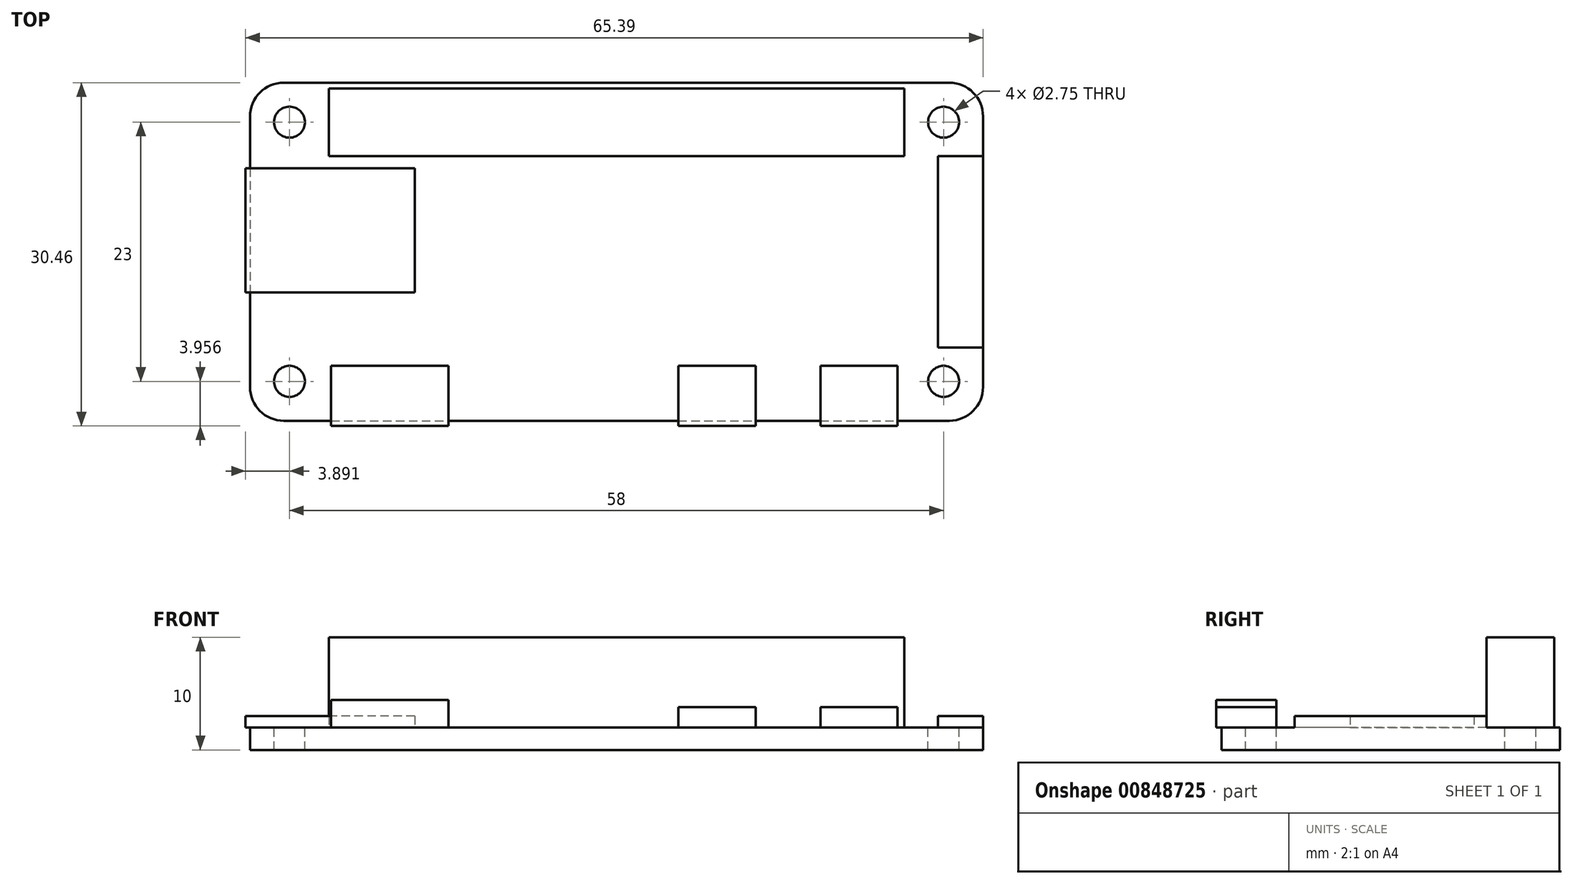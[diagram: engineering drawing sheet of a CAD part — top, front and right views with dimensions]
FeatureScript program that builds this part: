
annotation { "Feature Type Name" : "Feature", "Feature Type Description" : "" }
export const myFeature = defineFeature(function(context is Context, id is Id, definition is map)
    precondition{}
    {
        {
            var Q0;
            Q0=qCreatedBy(makeId("Top.planeOp"),FACE);
            var sketch = newSketch(context, id + "F0", { "sketchPlane" : qUnion([Q0])});
            skLineSegment(sketch, "E0.bottom", {"start": v(-40.48, 33.22) * mm, "end": v(24.52, 33.22) * mm});
            skLineSegment(sketch, "E0.top", {"start": v(-40.48, 3.22) * mm, "end": v(24.52, 3.22) * mm});
            skLineSegment(sketch, "E0.left", {"start": v(-40.48, 33.22) * mm, "end": v(-40.48, 3.22) * mm});
            skLineSegment(sketch, "E0.right", {"start": v(24.52, 33.22) * mm, "end": v(24.52, 3.22) * mm});
            skSolve(sketch);
        }
        {
            assignVariable(context, id + "F1", {"name" : "boardThickness", "anyValue" : 2});
        }
        {
            var Q0;
            Q0=makeQuery(id+"F0.imprint","IMPRINT",FACE,{"disambiguationData":[TD([[makeQuery(id+"F0.imprint","IMPRINT",EDGE,{"derivedFrom":sQuery(id+"F0.wireOp",EDGE,"E0.bottom")}),-1.0]])]});
            extrude(context, id + "F2", {"entities" : qUnion([Q0]), "depth" : (getVariable(context, 'boardThickness')) * mm, "offsetDistance" : 25 * mm});
        }
        {
            var Q0;
            Q0=makeQuery(id+"F2.opExtrude","SWEPT_EDGE",EDGE,{"disambiguationData":[OSD([sQuery(id+"F0.wireOp",EDGE,"E0.bottom"),sQuery(id+"F0.wireOp",EDGE,"E0.left")])]});
            var Q1;
            Q1=makeQuery(id+"F2.opExtrude","SWEPT_EDGE",EDGE,{"disambiguationData":[OSD([sQuery(id+"F0.wireOp",EDGE,"E0.top"),sQuery(id+"F0.wireOp",EDGE,"E0.left")])]});
            var Q2;
            Q2=makeQuery(id+"F2.opExtrude","SWEPT_EDGE",EDGE,{"disambiguationData":[OSD([sQuery(id+"F0.wireOp",EDGE,"E0.top"),sQuery(id+"F0.wireOp",EDGE,"E0.right")])]});
            var Q3;
            Q3=makeQuery(id+"F2.opExtrude","SWEPT_EDGE",EDGE,{"disambiguationData":[OSD([sQuery(id+"F0.wireOp",EDGE,"E0.bottom"),sQuery(id+"F0.wireOp",EDGE,"E0.right")])]});
            fillet(context, id + "F3", {"entities" : qUnion([Q0, Q1, Q2, Q3]), "radius" : 3 * mm, "tangentPropagation" : true, "allowEdgeOverflow" : false});
        }
        {
            var Q0;
            Q0=makeQuery(id+"F2.opExtrude","CAP_FACE",FACE,{"disambiguationData":[OSD([sQuery(id+"F0.wireOp",EDGE,"E0.bottom"),sQuery(id+"F0.wireOp",EDGE,"E0.top"),sQuery(id+"F0.wireOp",EDGE,"E0.left"),sQuery(id+"F0.wireOp",EDGE,"E0.right")])],"isStart":false});
            var sketch = newSketch(context, id + "F4", { "sketchPlane" : qUnion([Q0])});
            skCircle(sketch, "E1", {"center": v(21.02, 6.72) * mm, "radius": 1.38 * mm});
            skCircle(sketch, "E2", {"center": v(21.02, 29.72) * mm, "radius": 1.38 * mm});
            skCircle(sketch, "E3", {"center": v(-36.98, 29.72) * mm, "radius": 1.38 * mm});
            skCircle(sketch, "E4", {"center": v(-36.98, 6.72) * mm, "radius": 1.38 * mm});
            skCircle(sketch, "E5", {"center": v(21.02, 29.72) * mm, "radius": 3 * mm});
            skCircle(sketch, "E6", {"center": v(21.02, 6.72) * mm, "radius": 3 * mm});
            skCircle(sketch, "E7", {"center": v(-36.98, 6.72) * mm, "radius": 3 * mm});
            skCircle(sketch, "E8", {"center": v(-36.98, 29.72) * mm, "radius": 3 * mm});
            skSolve(sketch);
        }
        {
            var Q0;
            Q0=makeQuery(id+"F4.imprint","IMPRINT",FACE,{"disambiguationData":[TD([[makeQuery(id+"F4.imprint","IMPRINT",EDGE,{"derivedFrom":sQuery(id+"F4.wireOp",EDGE,"E2")}),1.0]])]});
            var Q1;
            Q1=makeQuery(id+"F4.imprint","IMPRINT",FACE,{"disambiguationData":[TD([[makeQuery(id+"F4.imprint","IMPRINT",EDGE,{"derivedFrom":sQuery(id+"F4.wireOp",EDGE,"E4")}),1.0]])]});
            var Q2;
            Q2=makeQuery(id+"F4.imprint","IMPRINT",FACE,{"disambiguationData":[TD([[makeQuery(id+"F4.imprint","IMPRINT",EDGE,{"derivedFrom":sQuery(id+"F4.wireOp",EDGE,"E3")}),1.0]])]});
            var Q3;
            Q3=makeQuery(id+"F4.imprint","IMPRINT",FACE,{"disambiguationData":[TD([[makeQuery(id+"F4.imprint","IMPRINT",EDGE,{"derivedFrom":sQuery(id+"F4.wireOp",EDGE,"E1")}),1.0]])]});
            extrude(context, id + "F5", {"entities" : qUnion([Q0, Q1, Q2, Q3]), "operationType" : NewBodyOperationType.REMOVE, "oppositeDirection" : true, "depth" : (getVariable(context, 'boardThickness')) * mm, "offsetDistance" : 25 * mm});
        }
        {
            assignVariable(context, id + "F6", {"name" : "miniHDMIh", "anyValue" : 2.42});
        }
        {
            assignVariable(context, id + "F7", {"name" : "microUSBh", "anyValue" : 1.8});
        }
        {
            var Q0;
            Q0=makeQuery(id+"F2.opExtrude","CAP_FACE",FACE,{"disambiguationData":[OSD([sQuery(id+"F0.wireOp",EDGE,"E0.bottom"),sQuery(id+"F0.wireOp",EDGE,"E0.top"),sQuery(id+"F0.wireOp",EDGE,"E0.left"),sQuery(id+"F0.wireOp",EDGE,"E0.right")])],"isStart":false});
            var sketch = newSketch(context, id + "F8", { "sketchPlane" : qUnion([Q0])});
            skLineSegment(sketch, "E9.bottom", {"start": v(-22.87, 2.76) * mm, "end": v(-33.29, 2.76) * mm});
            skLineSegment(sketch, "E9.top", {"start": v(-22.87, 8.09) * mm, "end": v(-33.29, 8.09) * mm});
            skLineSegment(sketch, "E9.left", {"start": v(-22.87, 2.76) * mm, "end": v(-22.87, 8.09) * mm});
            skLineSegment(sketch, "E9.right", {"start": v(-33.29, 2.76) * mm, "end": v(-33.29, 8.09) * mm});
            skPoint(sketch, "E9.middle", {"position": v(-28.08, 5.42) * mm});
            skLineSegment(sketch, "E10.bottom", {"start": v(16.95, 2.76) * mm, "end": v(10.1, 2.76) * mm});
            skLineSegment(sketch, "E10.top", {"start": v(16.95, 8.09) * mm, "end": v(10.1, 8.09) * mm});
            skLineSegment(sketch, "E10.left", {"start": v(16.95, 2.76) * mm, "end": v(16.95, 8.09) * mm});
            skLineSegment(sketch, "E10.right", {"start": v(10.1, 2.76) * mm, "end": v(10.1, 8.09) * mm});
            skPoint(sketch, "E10.middle", {"position": v(13.52, 5.42) * mm});
            skLineSegment(sketch, "E11.bottom", {"start": v(4.35, 2.76) * mm, "end": v(-2.5, 2.76) * mm});
            skLineSegment(sketch, "E11.top", {"start": v(4.35, 8.09) * mm, "end": v(-2.5, 8.09) * mm});
            skLineSegment(sketch, "E11.left", {"start": v(4.35, 2.76) * mm, "end": v(4.35, 8.09) * mm});
            skLineSegment(sketch, "E11.right", {"start": v(-2.5, 2.76) * mm, "end": v(-2.5, 8.09) * mm});
            skPoint(sketch, "E11.middle", {"position": v(0.92, 5.42) * mm});
            skLineSegment(sketch, "E12.bottom", {"start": v(-25.87, 14.62) * mm, "end": v(-40.87, 14.62) * mm});
            skLineSegment(sketch, "E12.top", {"start": v(-25.87, 25.62) * mm, "end": v(-40.87, 25.62) * mm});
            skLineSegment(sketch, "E12.left", {"start": v(-25.87, 14.62) * mm, "end": v(-25.87, 25.62) * mm});
            skLineSegment(sketch, "E12.right", {"start": v(-40.87, 14.62) * mm, "end": v(-40.87, 25.62) * mm});
            skPoint(sketch, "E12.middle", {"position": v(-33.37, 20.12) * mm});
            skLineSegment(sketch, "E13.bottom", {"start": v(20.52, 26.71) * mm, "end": v(24.52, 26.71) * mm});
            skLineSegment(sketch, "E13.top", {"start": v(20.52, 9.71) * mm, "end": v(24.52, 9.71) * mm});
            skLineSegment(sketch, "E13.left", {"start": v(20.52, 26.71) * mm, "end": v(20.52, 9.71) * mm});
            skLineSegment(sketch, "E13.right", {"start": v(24.52, 26.71) * mm, "end": v(24.52, 9.71) * mm});
            skSolve(sketch);
        }
        {
            var Q0;
            {var subQ0=sQuery(id+"F8.wireOp",EDGE,"E9.top");Q0=makeQuery(id+"F8.imprint","IMPRINT",FACE,{"disambiguationData":[TD([[makeQuery(id+"F8.imprint","IMPRINT",EDGE,{"derivedFrom":subQ0}),1.0]])]});}
            var Q1;
            {var subQ0=sQuery(id+"F8.wireOp",EDGE,"E9.bottom");Q1=makeQuery(id+"F8.imprint","IMPRINT",FACE,{"disambiguationData":[TD([[makeQuery(id+"F8.imprint","IMPRINT",EDGE,{"derivedFrom":subQ0}),-1.0]])]});}
            extrude(context, id + "F9", {"entities" : qUnion([Q0, Q1]), "operationType" : NewBodyOperationType.ADD, "depth" : (getVariable(context, 'miniHDMIh')) * mm, "offsetDistance" : 25 * mm});
        }
        {
            var Q0;
            {var subQ0=sQuery(id+"F8.wireOp",EDGE,"E11.top");Q0=makeQuery(id+"F8.imprint","IMPRINT",FACE,{"disambiguationData":[TD([[makeQuery(id+"F8.imprint","IMPRINT",EDGE,{"derivedFrom":subQ0}),1.0]])]});}
            var Q1;
            {var subQ0=sQuery(id+"F8.wireOp",EDGE,"E10.top");Q1=makeQuery(id+"F8.imprint","IMPRINT",FACE,{"disambiguationData":[TD([[makeQuery(id+"F8.imprint","IMPRINT",EDGE,{"derivedFrom":subQ0}),1.0]])]});}
            var Q2;
            {var subQ0=sQuery(id+"F8.wireOp",EDGE,"E11.bottom");Q2=makeQuery(id+"F8.imprint","IMPRINT",FACE,{"disambiguationData":[TD([[makeQuery(id+"F8.imprint","IMPRINT",EDGE,{"derivedFrom":subQ0}),-1.0]])]});}
            var Q3;
            {var subQ0=sQuery(id+"F8.wireOp",EDGE,"E10.bottom");Q3=makeQuery(id+"F8.imprint","IMPRINT",FACE,{"disambiguationData":[TD([[makeQuery(id+"F8.imprint","IMPRINT",EDGE,{"derivedFrom":subQ0}),-1.0]])]});}
            extrude(context, id + "F10", {"entities" : qUnion([Q0, Q1, Q2, Q3]), "operationType" : NewBodyOperationType.ADD, "depth" : (getVariable(context, 'microUSBh')) * mm, "offsetDistance" : 25 * mm});
        }
        {
            var Q0;
            Q0=makeQuery(id+"F8.imprint","IMPRINT",FACE,{"disambiguationData":[TD([[makeQuery(id+"F8.imprint","IMPRINT",EDGE,{"derivedFrom":sQuery(id+"F8.wireOp",EDGE,"E12.bottom")}),-1.0]])]});
            extrude(context, id + "F11", {"entities" : qUnion([Q0]), "operationType" : NewBodyOperationType.ADD, "depth" : 1 * mm, "offsetDistance" : 25 * mm});
        }
        {
            var Q0;
            Q0=makeQuery(id+"F8.imprint","IMPRINT",FACE,{"disambiguationData":[TD([[makeQuery(id+"F8.imprint","IMPRINT",EDGE,{"derivedFrom":sQuery(id+"F8.wireOp",EDGE,"E13.bottom")}),-1.0]])]});
            extrude(context, id + "F12", {"entities" : qUnion([Q0]), "operationType" : NewBodyOperationType.ADD, "depth" : 1 * mm, "offsetDistance" : 25 * mm});
        }
        {
            var Q0;
            {var subQ8=sQuery(id+"F8.wireOp",EDGE,"E9.top");Q0=makeQuery(id+"F8.imprint","IMPRINT",FACE,{"disambiguationData":[TD([[makeQuery(id+"F8.imprint","IMPRINT",EDGE,{"derivedFrom":subQ8}),-1.0]])]});}
            var sketch = newSketch(context, id + "F13", { "sketchPlane" : qUnion([Q0])});
            skLineSegment(sketch, "E14.bottom", {"start": v(17.52, 26.72) * mm, "end": v(-33.48, 26.72) * mm});
            skLineSegment(sketch, "E14.top", {"start": v(17.52, 32.72) * mm, "end": v(-33.48, 32.72) * mm});
            skLineSegment(sketch, "E14.left", {"start": v(17.52, 26.72) * mm, "end": v(17.52, 32.72) * mm});
            skLineSegment(sketch, "E14.right", {"start": v(-33.48, 26.72) * mm, "end": v(-33.48, 32.72) * mm});
            skPoint(sketch, "E14.middle", {"position": v(-7.98, 29.72) * mm});
            skLineSegment(sketch, "E15.bottom", {"start": v(17.52, 26.72) * mm, "end": v(12.52, 26.72) * mm});
            skLineSegment(sketch, "E15.top", {"start": v(17.52, 21.79) * mm, "end": v(12.52, 21.79) * mm});
            skLineSegment(sketch, "E15.left", {"start": v(17.52, 26.72) * mm, "end": v(17.52, 21.79) * mm});
            skLineSegment(sketch, "E15.right", {"start": v(12.52, 26.72) * mm, "end": v(12.52, 21.79) * mm});
            skSolve(sketch);
        }
        {
            assignVariable(context, id + "F14", {"name" : "pinHeight", "anyValue" : 8});
        }
        {
            var Q0;
            Q0=makeQuery(id+"F13.imprint","IMPRINT",FACE,{"disambiguationData":[TD([[makeQuery(id+"F13.imprint","IMPRINT",EDGE,{"derivedFrom":sQuery(id+"F13.wireOp",EDGE,"E14.bottom")}),-1.0]])]});
            var Q1;
            Q1=makeQuery(id+"F13.imprint","IMPRINT",FACE,{"disambiguationData":[TD([[makeQuery(id+"F13.imprint","IMPRINT",EDGE,{"derivedFrom":sQuery(id+"F13.wireOp",EDGE,"E15.bottom")}),1.0]])]});
            extrude(context, id + "F15", {"entities" : qUnion([Q0, Q1]), "operationType" : NewBodyOperationType.ADD, "depth" : (getVariable(context, 'pinHeight')) * mm, "offsetDistance" : 25 * mm});
        }
    });
